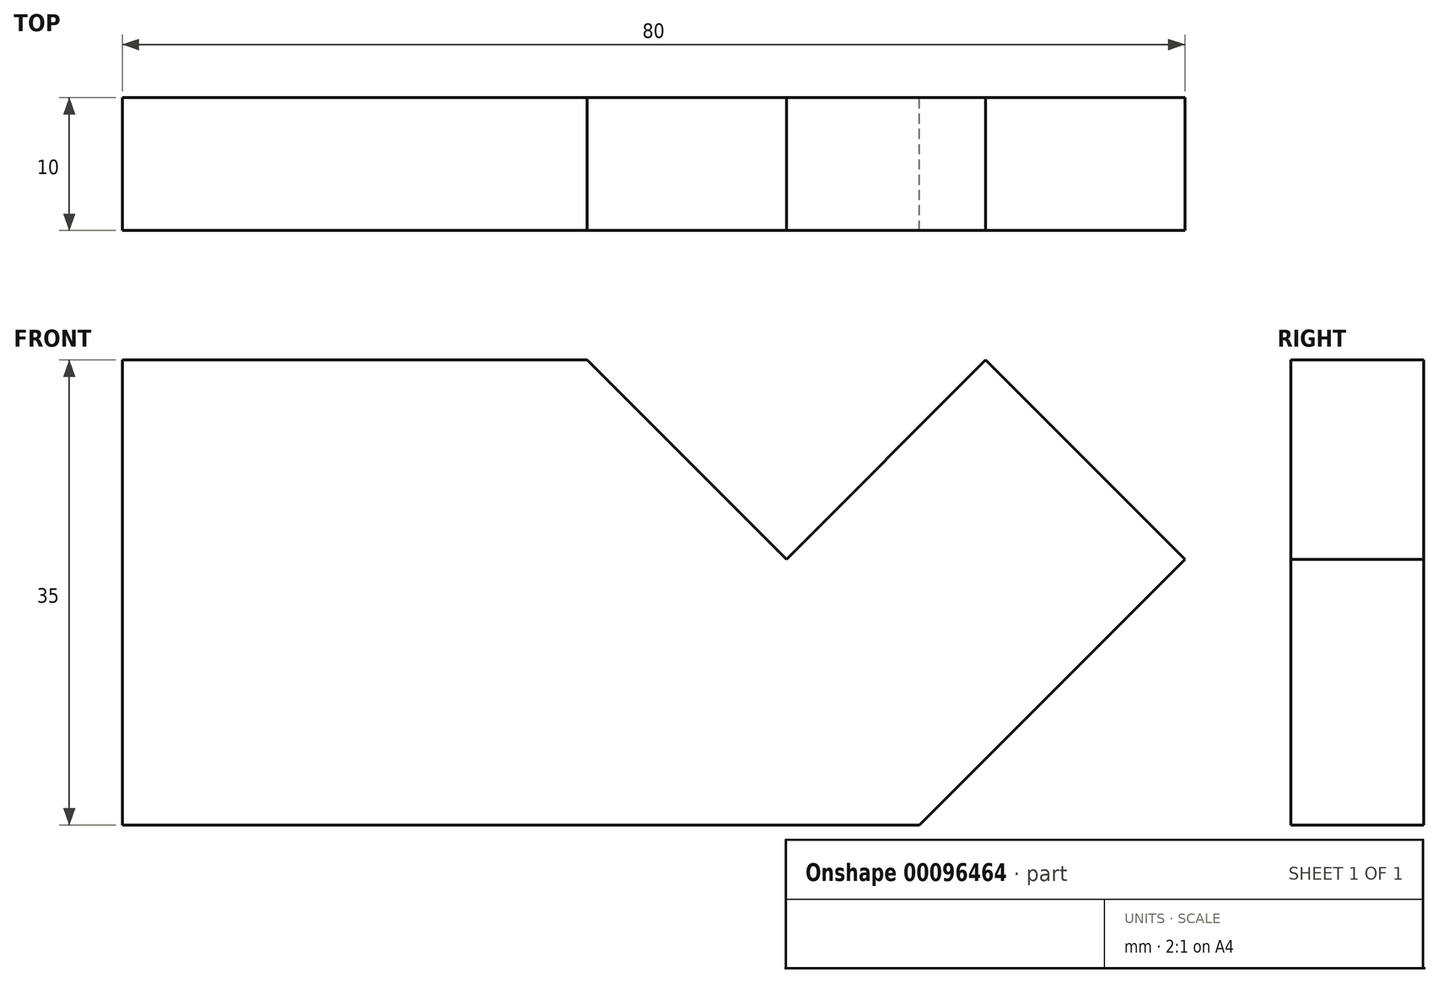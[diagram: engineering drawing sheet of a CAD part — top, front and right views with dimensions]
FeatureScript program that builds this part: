
annotation { "Feature Type Name" : "Feature", "Feature Type Description" : "" }
export const myFeature = defineFeature(function(context is Context, id is Id, definition is map)
    precondition{}
    {
        {
            var Q0;
            Q0=qCreatedBy(makeId("Front.planeOp"),FACE);
            var sketch = newSketch(context, id + "F0", { "sketchPlane" : qUnion([Q0])});
            skLineSegment(sketch, "E0", {"start": v(0, 0) * mm, "end": v(60, 0) * mm});
            skLineSegment(sketch, "E1", {"start": v(0, 0) * mm, "end": v(0, 35) * mm});
            skLineSegment(sketch, "E2", {"start": v(0, 35) * mm, "end": v(35, 35) * mm});
            skLineSegment(sketch, "E3", {"start": v(60, 0) * mm, "end": v(80, 20) * mm});
            skLineSegment(sketch, "E4", {"start": v(80, 20) * mm, "end": v(65, 35) * mm});
            skLineSegment(sketch, "E5", {"start": v(65, 35) * mm, "end": v(50, 20) * mm});
            skLineSegment(sketch, "E6", {"start": v(50, 20) * mm, "end": v(35, 35) * mm});
            skLineSegment(sketch, "E7", {"start": v(0, 35) * mm, "end": v(65, 35) * mm, "construction": true});
            skSolve(sketch);
        }
        {
            var Q0;
            Q0=makeQuery(id+"F0.imprint","IMPRINT",FACE,{"disambiguationData":[TD([[makeQuery(id+"F0.imprint","IMPRINT",EDGE,{"derivedFrom":sQuery(id+"F0.wireOp",EDGE,"E0")}),1.0]])]});
            extrude(context, id + "F1", {"entities" : qUnion([Q0]), "depth" : 10 * mm});
        }
    });
